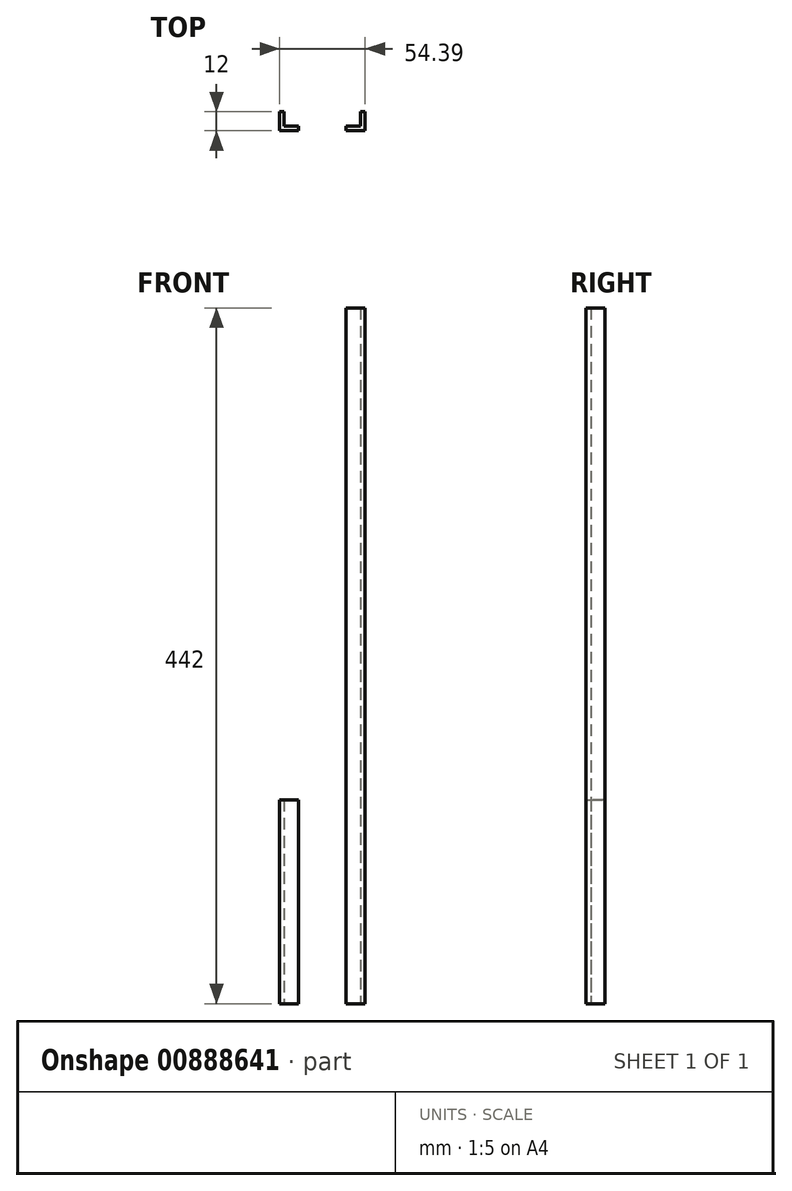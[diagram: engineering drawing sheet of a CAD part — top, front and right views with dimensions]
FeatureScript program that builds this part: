
annotation { "Feature Type Name" : "Feature", "Feature Type Description" : "" }
export const myFeature = defineFeature(function(context is Context, id is Id, definition is map)
    precondition{}
    {
        {
            var Q0;
            Q0=qCreatedBy(makeId("Top.planeOp"),FACE);
            var sketch = newSketch(context, id + "F0", { "sketchPlane" : qUnion([Q0])});
            skLineSegment(sketch, "E0", {"start": v(-26.83, 12) * mm, "end": v(-26.83, 0) * mm});
            skLineSegment(sketch, "E1", {"start": v(-26.83, 0) * mm, "end": v(-14.83, 0) * mm});
            skLineSegment(sketch, "E2", {"start": v(-14.83, 0) * mm, "end": v(-14.83, 3) * mm});
            skLineSegment(sketch, "E3", {"start": v(-14.83, 3) * mm, "end": v(-23.83, 3) * mm});
            skLineSegment(sketch, "E4", {"start": v(-23.83, 3) * mm, "end": v(-23.83, 12) * mm});
            skLineSegment(sketch, "E5", {"start": v(-23.83, 12) * mm, "end": v(-26.83, 12) * mm});
            skSolve(sketch);
        }
        {
            var Q0;
            Q0 = qSketchRegion(id + "F0", true);
            extrude(context, id + "F1", {"entities" : qUnion([Q0]), "depth" : 129.6 * mm, "offsetDistance" : 25 * mm});
        }
        {
            var Q0;
            Q0=qCreatedBy(makeId("Top.planeOp"),FACE);
            var sketch = newSketch(context, id + "F2", { "sketchPlane" : qUnion([Q0])});
            skLineSegment(sketch, "E6", {"start": v(15.56, 0) * mm, "end": v(27.56, 0) * mm});
            skLineSegment(sketch, "E7", {"start": v(27.56, 0) * mm, "end": v(27.56, 12) * mm});
            skLineSegment(sketch, "E8", {"start": v(27.56, 12) * mm, "end": v(24.56, 12) * mm});
            skLineSegment(sketch, "E9", {"start": v(24.56, 12) * mm, "end": v(24.56, 3) * mm});
            skLineSegment(sketch, "E10", {"start": v(24.56, 3) * mm, "end": v(15.56, 3) * mm});
            skLineSegment(sketch, "E11", {"start": v(15.56, 3) * mm, "end": v(15.56, 0) * mm});
            skSolve(sketch);
        }
        {
            var Q0;
            Q0 = qSketchRegion(id + "F2", true);
            extrude(context, id + "F3", {"entities" : qUnion([Q0]), "depth" : 442 * mm, "offsetDistance" : 25 * mm});
        }
    });
